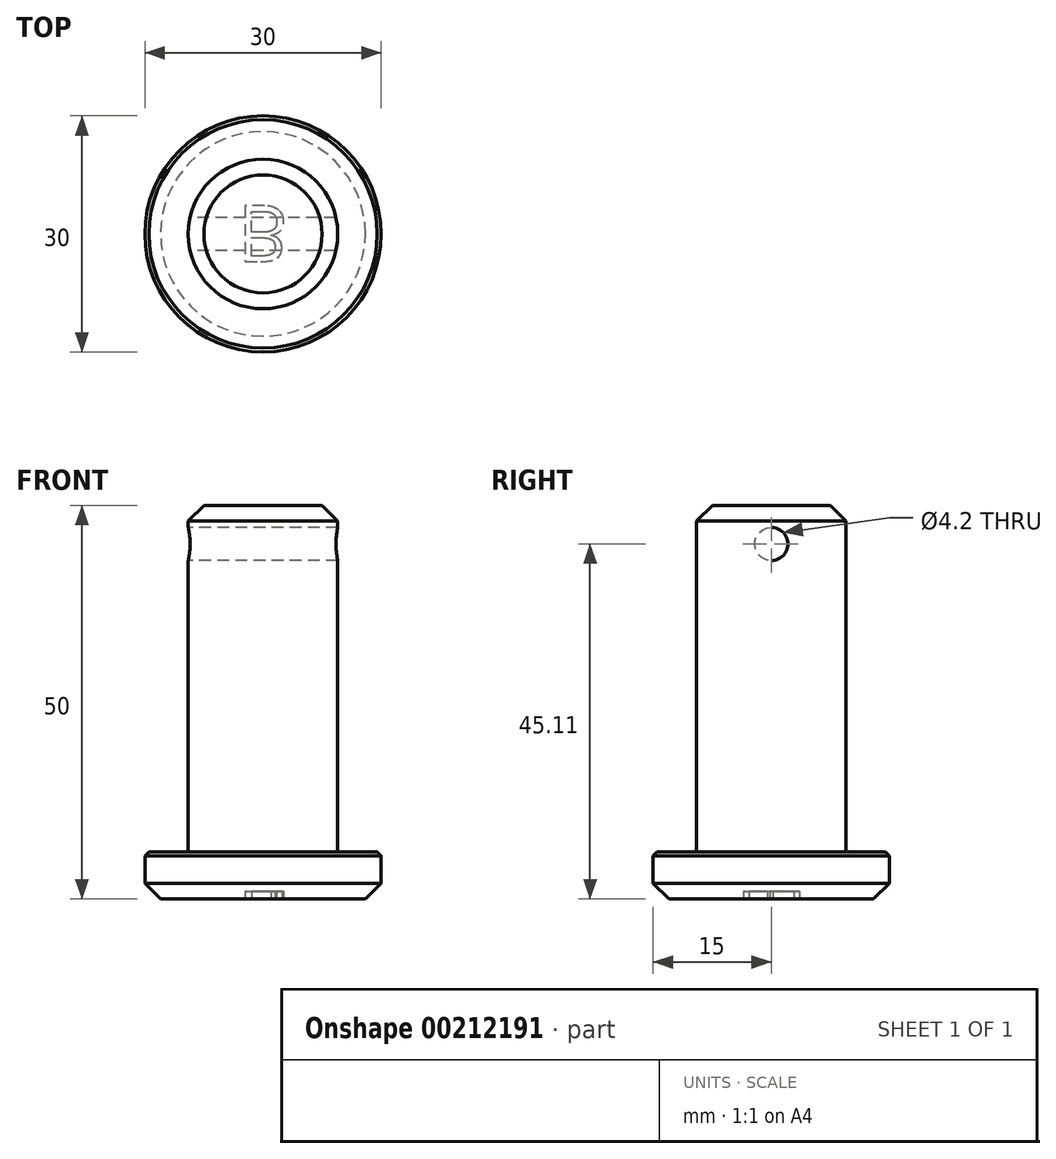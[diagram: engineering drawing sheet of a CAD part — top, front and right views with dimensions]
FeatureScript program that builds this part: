
annotation { "Feature Type Name" : "Feature", "Feature Type Description" : "" }
export const myFeature = defineFeature(function(context is Context, id is Id, definition is map)
    precondition{}
    {
        {
            var Q0;
            Q0=qCreatedBy(makeId("Top.planeOp"),FACE);
            var sketch = newSketch(context, id + "F0", { "sketchPlane" : qUnion([Q0])});
            skCircle(sketch, "E0", {"center": v(0, 0) * mm, "radius": 15 * mm});
            skCircle(sketch, "E1", {"center": v(0, 0) * mm, "radius": 9.5 * mm});
            skSolve(sketch);
        }
        {
            var Q0;
            Q0=makeQuery(id+"F0.imprint","IMPRINT",FACE,{"disambiguationData":[TD([[makeQuery(id+"F0.imprint","IMPRINT",EDGE,{"derivedFrom":sQuery(id+"F0.wireOp",EDGE,"E0")}),1.0]])]});
            extrude(context, id + "F1", {"entities" : qUnion([Q0]), "depth" : 6 * mm});
        }
        {
            var Q0;
            Q0=makeQuery(id+"F0.imprint","IMPRINT",FACE,{"disambiguationData":[TD([[makeQuery(id+"F0.imprint","IMPRINT",EDGE,{"derivedFrom":sQuery(id+"F0.wireOp",EDGE,"E1")}),1.0]])]});
            extrude(context, id + "F2", {"entities" : qUnion([Q0]), "operationType" : NewBodyOperationType.ADD, "depth" : 50 * mm});
        }
        {
            var Q0;
            Q0=qCreatedBy(makeId("Right.planeOp"),FACE);
            var sketch = newSketch(context, id + "F3", { "sketchPlane" : qUnion([Q0])});
            skCircle(sketch, "E2", {"center": v(0, 45.1) * mm, "radius": 2.1 * mm});
            skSolve(sketch);
        }
        {
            var Q0;
            Q0=sQuery(id+"F3.wireOp",VERTEX,"E2.center");
            var Q1;
            Q1=makeQuery(id+"F1.opExtrude","SWEPT_BODY",BODY,{"disambiguationData":[OSD([sQuery(id+"F0.wireOp",EDGE,"E0"),sQuery(id+"F0.wireOp",EDGE,"E1")])]});
            hole(context, id + "F4", {"style" : HoleStyle.SIMPLE, "endStyle" : HoleEndStyle.THROUGH, "oppositeDirection" : true, "standardTappedOrClearance" : lookupTablePath({ "standard" : "ISO", "size" : "4.2", "type" : "Drilled" }), "standardBlindInLast" : lookupTablePath({ "standard" : "ISO", "size" : "4.2", "type" : "Drilled" }), "holeDiameter" : 4.2 * mm, "locations" : qUnion([Q0]), "scope" : qUnion([Q1]), "tappedDepth" : 12 * mm, "tapClearance" : 3});
        }
        {
            var Q0;
            Q0=sQuery(id+"F3.wireOp",VERTEX,"E2.center");
            var Q1;
            Q1=makeQuery(id+"F1.opExtrude","SWEPT_BODY",BODY,{"disambiguationData":[OSD([sQuery(id+"F0.wireOp",EDGE,"E0"),sQuery(id+"F0.wireOp",EDGE,"E1")])]});
            hole(context, id + "F5", {"style" : HoleStyle.SIMPLE, "endStyle" : HoleEndStyle.THROUGH, "standardTappedOrClearance" : lookupTablePath({ "standard" : "ISO", "size" : "4.2", "type" : "Drilled" }), "standardBlindInLast" : lookupTablePath({ "standard" : "ISO", "size" : "4.2", "type" : "Drilled" }), "holeDiameter" : 4.2 * mm, "locations" : qUnion([Q0]), "scope" : qUnion([Q1]), "tappedDepth" : 12 * mm, "tapClearance" : 3});
        }
        {
            var Q0;
            Q0=makeQuery(id+"F2.opExtrude","CAP_EDGE",EDGE,{"disambiguationData":[OSD([sQuery(id+"F0.wireOp",EDGE,"E1")])],"isStart":false});
            var Q1;
            Q1=makeQuery(id+"F1.opExtrude","CAP_EDGE",EDGE,{"disambiguationData":[OSD([sQuery(id+"F0.wireOp",EDGE,"E0")])],"isStart":true});
            chamfer(context, id + "F6", {"entities" : qUnion([Q0, Q1]), "width" : 2 * mm, "tangentPropagation" : true});
        }
        {
            var Q0;
            Q0=makeQuery(id+"F5.hole-0.boolean.opBoolean","INTERSECT",EDGE,{"derivedFrom":[makeQuery(id+"F2.opExtrude","SWEPT_FACE",FACE,{"disambiguationData":[OSD([sQuery(id+"F0.wireOp",EDGE,"E1")])]}),makeQuery(id+"F5.hole-0.opRevolve","SWEPT_FACE",FACE,{"disambiguationData":[OSD([sQuery(id+"F5.hole-0.sketch.wireOp",EDGE,"core_line_2")])]})]});
            var Q1;
            Q1=makeQuery(id+"F4.hole-0.boolean.opBoolean","INTERSECT",EDGE,{"derivedFrom":[makeQuery(id+"F2.opExtrude","SWEPT_FACE",FACE,{"disambiguationData":[OSD([sQuery(id+"F0.wireOp",EDGE,"E1")])]}),makeQuery(id+"F4.hole-0.opRevolve","SWEPT_FACE",FACE,{"disambiguationData":[OSD([sQuery(id+"F4.hole-0.sketch.wireOp",EDGE,"core_line_2")])]})]});
            var Q2;
            Q2=makeQuery(id+"F1.opExtrude","CAP_EDGE",EDGE,{"disambiguationData":[OSD([sQuery(id+"F0.wireOp",EDGE,"E0")])],"isStart":false});
            chamfer(context, id + "F7", {"entities" : qUnion([Q0, Q1, Q2]), "width" : .5 * mm, "tangentPropagation" : true});
        }
        {
            var Q0;
            {var subQ0=sQuery(id+"F0.wireOp",EDGE,"E1");Q0=makeQuery(id+"F2.boolean.opBoolean","MERGE",FACE,{"derivedFrom":[makeQuery(id+"F1.opExtrude","CAP_FACE",FACE,{"disambiguationData":[OSD([sQuery(id+"F0.wireOp",EDGE,"E0"),subQ0])],"isStart":true}),makeQuery(id+"F2.opExtrude","CAP_FACE",FACE,{"disambiguationData":[OSD([subQ0])],"isStart":true})]});}
            var sketch = newSketch(context, id + "F8", { "sketchPlane" : qUnion([Q0])});
            skLineSegment(sketch, "E3.bottom", {"start": v(-3.26, -3.57) * mm, "end": v(3.26, -3.57) * mm, "construction": true});
            skLineSegment(sketch, "E3.top", {"start": v(-3.26, 3.57) * mm, "end": v(3.26, 3.57) * mm, "construction": true});
            skLineSegment(sketch, "E3.left", {"start": v(-3.26, -3.57) * mm, "end": v(-3.26, 3.57) * mm, "construction": true});
            skLineSegment(sketch, "E3.right", {"start": v(3.26, -3.57) * mm, "end": v(3.26, 3.57) * mm, "construction": true});
            skPoint(sketch, "E3.middle", {"position": v(0, 0) * mm});
            skText(sketch, "E4", { "text": "B", "fontName": "OpenSans-Regular.ttf"});
            const initialGuessF8  = {"E4": [-0.00326, -0.00357, 1, 0, 0.00715]};
            skSetInitialGuess(sketch, initialGuessF8);
            skSolve(sketch);
        }
        {
            var Q0;
            Q0=makeQuery(id+"F8.imprint","IMPRINT",FACE,{"disambiguationData":[TD([[makeQuery(id+"F8.imprint","IMPRINT",EDGE,{"derivedFrom":sQuery(id+"F8.wireOp",EDGE,"E4.sketch_text.stroke-0")}),-1.0]])]});
            extrude(context, id + "F9", {"entities" : qUnion([Q0]), "operationType" : NewBodyOperationType.REMOVE, "oppositeDirection" : true, "depth" : 1 * mm});
        }
    });
